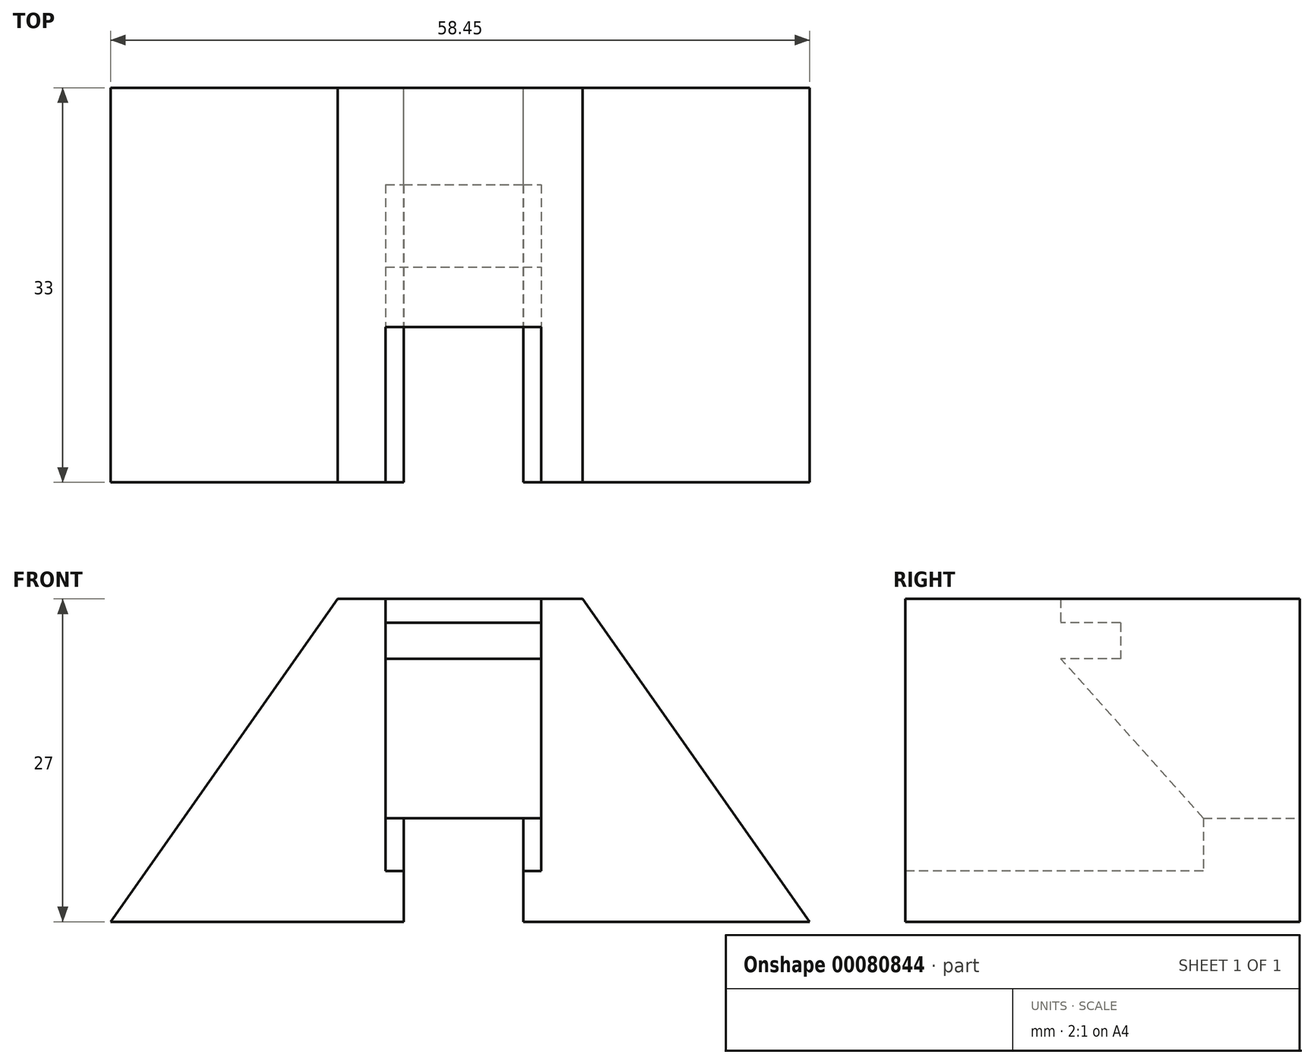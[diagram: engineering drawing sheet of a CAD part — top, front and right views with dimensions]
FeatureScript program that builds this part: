
annotation { "Feature Type Name" : "Feature", "Feature Type Description" : "" }
export const myFeature = defineFeature(function(context is Context, id is Id, definition is map)
    precondition{}
    {
        {
            var Q0;
            Q0=qCreatedBy(makeId("Front.planeOp"),FACE);
            var sketch = newSketch(context, id + "F0", { "sketchPlane" : qUnion([Q0])});
            skLineSegment(sketch, "E0", {"start": v(-29.5, 0) * mm, "end": v(-5, 0) * mm});
            skLineSegment(sketch, "E1", {"start": v(28.95, 0) * mm, "end": v(9.97, 27) * mm});
            skLineSegment(sketch, "E2", {"start": v(9.97, 27) * mm, "end": v(-10.53, 27) * mm});
            skLineSegment(sketch, "E3", {"start": v(-10.53, 27) * mm, "end": v(-29.5, 0) * mm});
            skLineSegment(sketch, "E4.top", {"start": v(-5, 8.67) * mm, "end": v(5, 8.67) * mm});
            skLineSegment(sketch, "E4.left", {"start": v(-5, 0) * mm, "end": v(-5, 8.67) * mm});
            skLineSegment(sketch, "E4.right", {"start": v(5, 0) * mm, "end": v(5, 8.67) * mm});
            skLineSegment(sketch, "E5.trimOffspring", {"start": v(5, 0) * mm, "end": v(28.95, 0) * mm});
            skSolve(sketch);
        }
        {
            var Q0;
            Q0 = qSketchRegion(id + "F0", true);
            extrude(context, id + "F1", {"entities" : qUnion([Q0]), "depth" : 33 * mm});
        }
        {
            var Q0;
            Q0=makeQuery(id+"F1.opExtrude","CAP_FACE",FACE,{"disambiguationData":[OSD([sQuery(id+"F0.wireOp",EDGE,"E0"),sQuery(id+"F0.wireOp",EDGE,"E1"),sQuery(id+"F0.wireOp",EDGE,"E2"),sQuery(id+"F0.wireOp",EDGE,"E3"),sQuery(id+"F0.wireOp",EDGE,"E4.top"),sQuery(id+"F0.wireOp",EDGE,"E4.left"),sQuery(id+"F0.wireOp",EDGE,"E4.right"),sQuery(id+"F0.wireOp",EDGE,"E5.trimOffspring")])],"isStart":false});
            var sketch = newSketch(context, id + "F2", { "sketchPlane" : qUnion([Q0])});
            skLineSegment(sketch, "E6.bottom", {"start": v(-6.5, 27) * mm, "end": v(6.5, 27) * mm});
            skLineSegment(sketch, "E6.top", {"start": v(-6.5, 4.25) * mm, "end": v(6.5, 4.25) * mm});
            skLineSegment(sketch, "E6.left", {"start": v(-6.5, 27) * mm, "end": v(-6.5, 4.25) * mm});
            skLineSegment(sketch, "E6.right", {"start": v(6.5, 27) * mm, "end": v(6.5, 4.25) * mm});
            skSolve(sketch);
        }
        {
            var Q0;
            Q0 = qSketchRegion(id + "F2", true);
            extrude(context, id + "F3", {"entities" : qUnion([Q0]), "operationType" : NewBodyOperationType.REMOVE, "oppositeDirection" : true, "depth" : 13 * mm});
        }
        {
            var Q0;
            Q0=makeQuery(id+"F3.boolean.opBoolean","COPY",FACE,{"derivedFrom":makeQuery(id+"F3.opExtrude","CAP_FACE",FACE,{"disambiguationData":[OSD([sQuery(id+"F2.wireOp",EDGE,"E6.bottom"),sQuery(id+"F2.wireOp",EDGE,"E6.top"),sQuery(id+"F2.wireOp",EDGE,"E6.left"),sQuery(id+"F2.wireOp",EDGE,"E6.right")])],"isStart":false})});
            var sketch = newSketch(context, id + "F4", { "sketchPlane" : qUnion([Q0])});
            skLineSegment(sketch, "E7.bottom", {"start": v(-6.5, 25) * mm, "end": v(6.5, 25) * mm});
            skLineSegment(sketch, "E7.top", {"start": v(-6.5, 22) * mm, "end": v(6.5, 22) * mm});
            skLineSegment(sketch, "E7.left", {"start": v(-6.5, 25) * mm, "end": v(-6.5, 22) * mm});
            skLineSegment(sketch, "E7.right", {"start": v(6.5, 25) * mm, "end": v(6.5, 22) * mm});
            skSolve(sketch);
        }
        {
            var Q0;
            Q0 = qSketchRegion(id + "F4", true);
            extrude(context, id + "F5", {"entities" : qUnion([Q0]), "operationType" : NewBodyOperationType.REMOVE, "oppositeDirection" : true, "depth" : 5 * mm});
        }
        {
            var Q0;
            Q0=qCreatedBy(makeId("Right.planeOp"),FACE);
            var sketch = newSketch(context, id + "F6", { "sketchPlane" : qUnion([Q0])});
            skLineSegment(sketch, "E8", {"start": v(-20, 22) * mm, "end": v(-20, 4.25) * mm});
            skLineSegment(sketch, "E9", {"start": v(-20, 4.25) * mm, "end": v(-8.1, 4.25) * mm});
            skLineSegment(sketch, "E10", {"start": v(-8.09, 4.25) * mm, "end": v(-8.1, 8.67) * mm});
            skLineSegment(sketch, "E11", {"start": v(-8.1, 8.67) * mm, "end": v(-20, 22) * mm});
            skSolve(sketch);
        }
        {
            var Q0;
            Q0 = qSketchRegion(id + "F6", true);
            extrude(context, id + "F7", {"entities" : qUnion([Q0]), "operationType" : NewBodyOperationType.REMOVE, "endBound" : BoundingType.SYMMETRIC, "oppositeDirection" : true, "depth" : 13 * mm});
        }
    });
